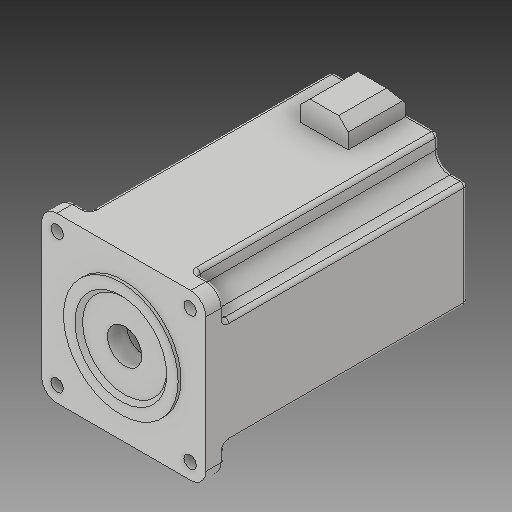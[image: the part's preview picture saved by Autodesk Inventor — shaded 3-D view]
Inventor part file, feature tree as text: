
AUTODESK INVENTOR PART (.ipt)
format: ipt  version: 2018 (Build 220112000, 112)  size: 388,096 bytes
history: native  units: mm
features: extrude x13, sketch x13, chamfer x5, projected_geometry x4, fillet x3, hole x1, plane x1
ambient origin geometry x8: Origin, YZ Plane, XZ Plane, XY Plane, X Axis, Y Axis, Z Axis, Center Point
bodies: Solid1 (feature_tree)
feature tree (40):
  extrude  "Extrusion1"  Depth=86.0mm
  extrude  "Extrusion2"  Depth=140.0mm
  extrude  "Extrusion3"  Depth=1.5mm
  hole  "Hole1"  [1 undecoded]
  plane  "Work Plane1"
  extrude  "Extrusion4"  Depth=13.0mm TaperAngle=0.0deg
  sketch  "Sketch6"  dims[d13=3.0mm d14=6.0mm d15=4.0mm d16=2.0mm d17=90.0deg d18=13.0mm d19=0.0mm d24=2.438mm d25=0.0mm]
  extrude  "Extrusion6"  Depth=69.6mm
  extrude  "Extrusion7"  Depth=120.0mm TaperAngle=0.0deg
  chamfer  "Chamfer1"  Distance=13.0mm
  fillet  "Fillet1"  Radius=8.0mm
  chamfer  "Chamfer2"  Distance=5.0mm Angle=45.0deg
  chamfer  "Chamfer3"  Distance=1.0mm Angle=45.0deg
  extrude  "Extrusion8"  Depth=56.0mm
  extrude  "Extrusion9"  Depth=3.0mm TaperAngle=45.0deg
  chamfer  "Chamfer4"  Distance=2.0mm
  fillet  "Fillet3"  Radius=15.0mm
  extrude  "Extrusion10"  Depth=15.0mm
  fillet  "Fillet4"  Radius=40.0mm
  extrude  "Extrusion11"  Depth=130.0mm TaperAngle=0.0deg
  chamfer  "Chamfer5"  Distance=2.0mm
  extrude  "Extrusion13"  Depth=8.0mm
  extrude  "Extrusion14"  Depth=2.0mm TaperAngle=0.0deg
  extrude  "Extrusion15"  Depth=2.0mm TaperAngle=45.0deg
  sketch  "Sketch1"  dims[d0=86.0mm d1=86.0mm]
  sketch  "Sketch2"  dims[d2=140.0mm d3=0.0mm d5=60.0mm]
  sketch  "Sketch3"  dims[d6=1.5mm d7=0.0mm d8=14.0mm]
  sketch  "Sketch5"  dims[d9=40.0mm d10=0.0mm d11=10.0mm d12=10.0mm]
  projected_geometry  "Projected Loop1"
  sketch  "Sketch7"  dims[d36=6.5mm d37=69.6mm]
  projected_geometry  "Projected Loop2"
  sketch  "Sketch8"  dims[d38=69.6mm d39=120.0mm d40=0.0mm]
  sketch  "Sketch9"  dims[d41=25.0mm]
  projected_geometry  "Projected Loop3"
  sketch  "Sketch10"  dims[d42=30.0mm]
  sketch  "Sketch11"  dims[d43=5.0mm d46=13.0mm d47=0.0mm]
  sketch  "Sketch13"  dims[d48=5.0mm d49=7.0mm d50=45.0deg d51=8.0mm d53=5.0mm d54=7.0mm d55=45.0deg d56=1.0mm d57=7.0mm d58=45.0deg]
  projected_geometry  "Projected Loop5"
  sketch  "Sketch14"  dims[d59=3.0mm d60=0.0mm d61=56.0mm]
  sketch  "Sketch15"  dims[d62=3.0mm d63=0.0mm d64=3.0mm d65=7.0mm d66=45.0deg d67=2.0mm d71=15.0mm d72=15.0mm d73=40.0mm d75=360.0deg d77=130.0mm d78=0.0mm d79=2.0mm d81=8.0mm d82=2.0mm d83=0.0mm d84=2.0mm d85=7.0mm d86=45.0deg d90=13.0mm d91=10.0mm d92=0.0mm d93=10.0mm d94=0.0mm d95=10.0mm d96=0.0mm]
note: 1 required parameter value undecoded (feature->parameter linkage not recoverable at this tier; creation-order binding heuristic only, values carry confidence <= 0.55)
